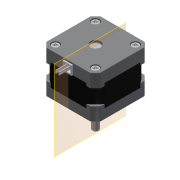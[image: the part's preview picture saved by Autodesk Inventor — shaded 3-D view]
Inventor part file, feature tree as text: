
AUTODESK INVENTOR PART (.ipt)
format: ipt  version: 2019.4 (Build 234330000, 330)  size: 1,435,648 bytes
history: native  units: mm
features: plane x1
ambient origin geometry x8: Origin, YZ Plane, XZ Plane, XY Plane, X Axis, Y Axis, Z Axis, Center Point
bodies: Solid1 (feature_tree), Solid2 (feature_tree), Solid3 (feature_tree), Solid4 (feature_tree), Solid5 (feature_tree), Solid6 (feature_tree), Solid7 (feature_tree), Solid8 (feature_tree), Solid9 (feature_tree), Solid10 (feature_tree), Solid11 (feature_tree), Solid12 (feature_tree)
feature tree (1):
  plane  "Work Plane1"
